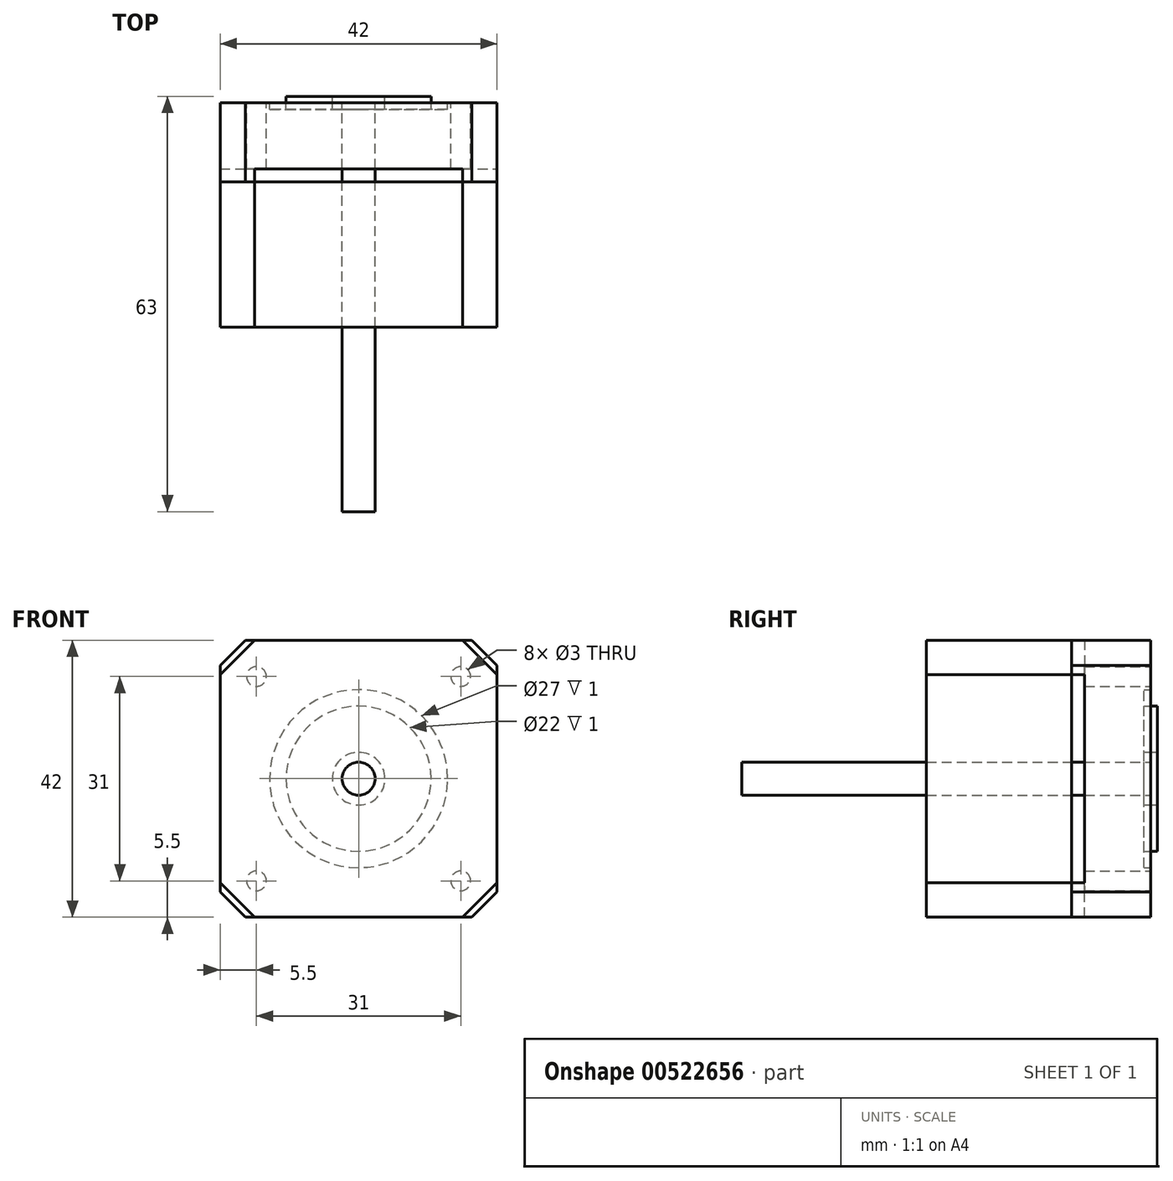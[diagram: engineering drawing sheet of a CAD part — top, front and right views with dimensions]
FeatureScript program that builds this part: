
annotation { "Feature Type Name" : "Feature", "Feature Type Description" : "" }
export const myFeature = defineFeature(function(context is Context, id is Id, definition is map)
    precondition{}
    {
        {
            var Q0;
            Q0=qCreatedBy(makeId("Front.planeOp"),FACE);
            var sketch = newSketch(context, id + "F0", { "sketchPlane" : qUnion([Q0])});
            skCircle(sketch, "E0", {"center": v(0, 0) * mm, "radius": 2.5 * mm});
            skCircle(sketch, "E1", {"center": v(0, 0) * mm, "radius": 11 * mm});
            skCircle(sketch, "E2", {"center": v(0, 0) * mm, "radius": 4 * mm});
            skCircle(sketch, "E3", {"center": v(0, 0) * mm, "radius": 13.5 * mm});
            skLineSegment(sketch, "E4.bottom", {"start": v(-17.18, 21) * mm, "end": v(17.18, 21) * mm});
            skLineSegment(sketch, "E4.top", {"start": v(-17.18, -21) * mm, "end": v(17.18, -21) * mm});
            skLineSegment(sketch, "E4.left", {"start": v(-21, 17.18) * mm, "end": v(-21, -17.18) * mm});
            skLineSegment(sketch, "E4.right", {"start": v(21, 17.18) * mm, "end": v(21, -17.18) * mm});
            skCircle(sketch, "E5", {"center": v(-15.5, 15.5) * mm, "radius": 1.5 * mm});
            skCircle(sketch, "E6", {"center": v(15.5, 15.5) * mm, "radius": 1.5 * mm});
            skCircle(sketch, "E7", {"center": v(15.5, -15.5) * mm, "radius": 1.5 * mm});
            skCircle(sketch, "E8", {"center": v(-15.5, -15.5) * mm, "radius": 1.5 * mm});
            skPoint(sketch, "E9.visualSharp", {"position": v(-21, 21) * mm});
            skPoint(sketch, "E10.visualSharp", {"position": v(21, 21) * mm});
            skPoint(sketch, "E11.visualSharp", {"position": v(21, -21) * mm});
            skPoint(sketch, "E12.visualSharp", {"position": v(-21, -21) * mm});
            skLineSegment(sketch, "E13", {"start": v(-21, -17.18) * mm, "end": v(-17.18, -21) * mm});
            skLineSegment(sketch, "E14", {"start": v(17.18, 21) * mm, "end": v(21, 17.18) * mm});
            skLineSegment(sketch, "E15", {"start": v(21, -17.18) * mm, "end": v(17.18, -21) * mm});
            skLineSegment(sketch, "E16", {"start": v(-21, 17.18) * mm, "end": v(-17.18, 21) * mm});
            skSolve(sketch);
        }
        {
            var Q0;
            Q0=makeQuery(id+"F0.imprint","IMPRINT",FACE,{"disambiguationData":[TD([[makeQuery(id+"F0.imprint","IMPRINT",EDGE,{"derivedFrom":sQuery(id+"F0.wireOp",EDGE,"E3")}),-1.0]])]});
            var Q1;
            Q1=makeQuery(id+"F0.imprint","IMPRINT",FACE,{"disambiguationData":[TD([[makeQuery(id+"F0.imprint","IMPRINT",EDGE,{"derivedFrom":sQuery(id+"F0.wireOp",EDGE,"E1")}),-1.0]])]});
            var Q2;
            Q2=makeQuery(id+"F0.imprint","IMPRINT",FACE,{"disambiguationData":[TD([[makeQuery(id+"F0.imprint","IMPRINT",EDGE,{"derivedFrom":sQuery(id+"F0.wireOp",EDGE,"E1")}),1.0]])]});
            var Q3;
            Q3=makeQuery(id+"F0.imprint","IMPRINT",FACE,{"disambiguationData":[TD([[makeQuery(id+"F0.imprint","IMPRINT",EDGE,{"derivedFrom":sQuery(id+"F0.wireOp",EDGE,"E0")}),1.0]])]});
            var Q4;
            Q4=makeQuery(id+"F0.imprint","IMPRINT",FACE,{"disambiguationData":[TD([[makeQuery(id+"F0.imprint","IMPRINT",EDGE,{"derivedFrom":sQuery(id+"F0.wireOp",EDGE,"E0")}),-1.0]])]});
            extrude(context, id + "F1", {"entities" : qUnion([Q0, Q1, Q2, Q3, Q4]), "depth" : 12 * mm, "offsetDistance" : 25 * mm});
        }
        {
            var Q0;
            Q0=makeQuery(id+"F0.imprint","IMPRINT",FACE,{"disambiguationData":[TD([[makeQuery(id+"F0.imprint","IMPRINT",EDGE,{"derivedFrom":sQuery(id+"F0.wireOp",EDGE,"E1")}),-1.0]])]});
            var Q1;
            Q1=makeQuery(id+"F0.imprint","IMPRINT",FACE,{"disambiguationData":[TD([[makeQuery(id+"F0.imprint","IMPRINT",EDGE,{"derivedFrom":sQuery(id+"F0.wireOp",EDGE,"E0")}),-1.0]])]});
            extrude(context, id + "F2", {"entities" : qUnion([Q0, Q1]), "operationType" : NewBodyOperationType.REMOVE, "depth" : 1 * mm, "offsetDistance" : 25 * mm});
        }
        {
            var Q0;
            Q0=makeQuery(id+"F0.imprint","IMPRINT",FACE,{"disambiguationData":[TD([[makeQuery(id+"F0.imprint","IMPRINT",EDGE,{"derivedFrom":sQuery(id+"F0.wireOp",EDGE,"E1")}),1.0]])]});
            extrude(context, id + "F3", {"entities" : qUnion([Q0]), "operationType" : NewBodyOperationType.ADD, "oppositeDirection" : true, "depth" : 1 * mm, "offsetDistance" : 25 * mm});
        }
        {
            var Q0;
            Q0=makeQuery(id+"F0.imprint","IMPRINT",FACE,{"disambiguationData":[TD([[makeQuery(id+"F0.imprint","IMPRINT",EDGE,{"derivedFrom":sQuery(id+"F0.wireOp",EDGE,"E0")}),1.0]])]});
            extrude(context, id + "F4", {"entities" : qUnion([Q0]), "operationType" : NewBodyOperationType.REMOVE, "depth" : 20 * mm, "offsetDistance" : 25 * mm});
        }
        {
            var Q0;
            Q0=makeQuery(id+"F1.opExtrude","CAP_FACE",FACE,{"disambiguationData":[OSD([sQuery(id+"F0.wireOp",EDGE,"E4.bottom"),sQuery(id+"F0.wireOp",EDGE,"E4.top"),sQuery(id+"F0.wireOp",EDGE,"E4.left"),sQuery(id+"F0.wireOp",EDGE,"E4.right"),sQuery(id+"F0.wireOp",EDGE,"E5"),sQuery(id+"F0.wireOp",EDGE,"E6"),sQuery(id+"F0.wireOp",EDGE,"E7"),sQuery(id+"F0.wireOp",EDGE,"E8"),sQuery(id+"F0.wireOp",EDGE,"E13"),sQuery(id+"F0.wireOp",EDGE,"E14"),sQuery(id+"F0.wireOp",EDGE,"E15"),sQuery(id+"F0.wireOp",EDGE,"E16")])],"isStart":false});
            var sketch = newSketch(context, id + "F5", { "sketchPlane" : qUnion([Q0])});
            skLineSegment(sketch, "E17.0", {"start": v(15.77, 21) * mm, "end": v(21, 15.77) * mm});
            skLineSegment(sketch, "E18.0", {"start": v(21, 15.77) * mm, "end": v(21, -15.77) * mm});
            skLineSegment(sketch, "E19", {"start": v(21, -15.77) * mm, "end": v(15.77, -21) * mm});
            skLineSegment(sketch, "E20", {"start": v(15.77, -21) * mm, "end": v(-15.77, -21) * mm});
            skLineSegment(sketch, "E21", {"start": v(-15.77, -21) * mm, "end": v(-21, -15.77) * mm});
            skLineSegment(sketch, "E22", {"start": v(-21, -15.77) * mm, "end": v(-21, 15.77) * mm});
            skLineSegment(sketch, "E23", {"start": v(-21, 15.77) * mm, "end": v(-15.77, 21) * mm});
            skLineSegment(sketch, "E24", {"start": v(-15.77, 21) * mm, "end": v(15.77, 21) * mm});
            skLineSegment(sketch, "E25", {"start": v(21, 0) * mm, "end": v(-21, 0) * mm, "construction": true});
            skLineSegment(sketch, "E26", {"start": v(0, 21) * mm, "end": v(0, -21) * mm, "construction": true});
            skCircle(sketch, "E27.0", {"center": v(0, 0) * mm, "radius": 2.5 * mm});
            skSolve(sketch);
        }
        {
            var Q0;
            Q0 = qSketchRegion(id + "F5", true);
            extrude(context, id + "F6", {"entities" : qUnion([Q0]), "operationType" : NewBodyOperationType.REMOVE, "oppositeDirection" : true, "depth" : 2 * mm, "offsetDistance" : 25 * mm});
        }
        {
            var Q0;
            Q0 = qSketchRegion(id + "F5", true);
            extrude(context, id + "F7", {"entities" : qUnion([Q0]), "depth" : 22 * mm, "offsetDistance" : 25 * mm, "hasSecondDirection" : true, "secondDirectionOppositeDirection" : true, "secondDirectionDepth" : 2 * mm});
        }
        {
            var Q0;
            Q0=makeQuery(id+"F0.imprint","IMPRINT",FACE,{"disambiguationData":[TD([[makeQuery(id+"F0.imprint","IMPRINT",EDGE,{"derivedFrom":sQuery(id+"F0.wireOp",EDGE,"E3")}),-1.0]])]});
            var Q1;
            Q1=makeQuery(id+"F0.imprint","IMPRINT",FACE,{"disambiguationData":[TD([[makeQuery(id+"F0.imprint","IMPRINT",EDGE,{"derivedFrom":sQuery(id+"F0.wireOp",EDGE,"E1")}),-1.0]])]});
            var Q2;
            Q2=makeQuery(id+"F0.imprint","IMPRINT",FACE,{"disambiguationData":[TD([[makeQuery(id+"F0.imprint","IMPRINT",EDGE,{"derivedFrom":sQuery(id+"F0.wireOp",EDGE,"E1")}),1.0]])]});
            var Q3;
            Q3=makeQuery(id+"F0.imprint","IMPRINT",FACE,{"disambiguationData":[TD([[makeQuery(id+"F0.imprint","IMPRINT",EDGE,{"derivedFrom":sQuery(id+"F0.wireOp",EDGE,"E0")}),-1.0]])]});
            extrude(context, id + "F8", {"entities" : qUnion([Q0, Q1, Q2, Q3]), "depth" : 12 * mm, "offsetDistance" : 25 * mm});
        }
        {
            var Q0;
            Q0=makeQuery(id+"F0.imprint","IMPRINT",FACE,{"disambiguationData":[TD([[makeQuery(id+"F0.imprint","IMPRINT",EDGE,{"derivedFrom":sQuery(id+"F0.wireOp",EDGE,"E1")}),1.0]])]});
            extrude(context, id + "F9", {"entities" : qUnion([Q0]), "operationType" : NewBodyOperationType.REMOVE, "depth" : 1 * mm, "offsetDistance" : 25 * mm});
        }
        {
            var Q0;
            Q0 = qSketchRegion(id + "F5", true);
            extrude(context, id + "F10", {"entities" : qUnion([Q0]), "operationType" : NewBodyOperationType.REMOVE, "oppositeDirection" : true, "depth" : 2 * mm, "offsetDistance" : 25 * mm});
        }
        {
            var Q0;
            Q0=makeQuery(id+"F0.imprint","IMPRINT",FACE,{"disambiguationData":[TD([[makeQuery(id+"F0.imprint","IMPRINT",EDGE,{"derivedFrom":sQuery(id+"F0.wireOp",EDGE,"E0")}),1.0]])]});
            extrude(context, id + "F11", {"entities" : qUnion([Q0]), "depth" : 62 * mm, "offsetDistance" : 25 * mm});
        }
    });
